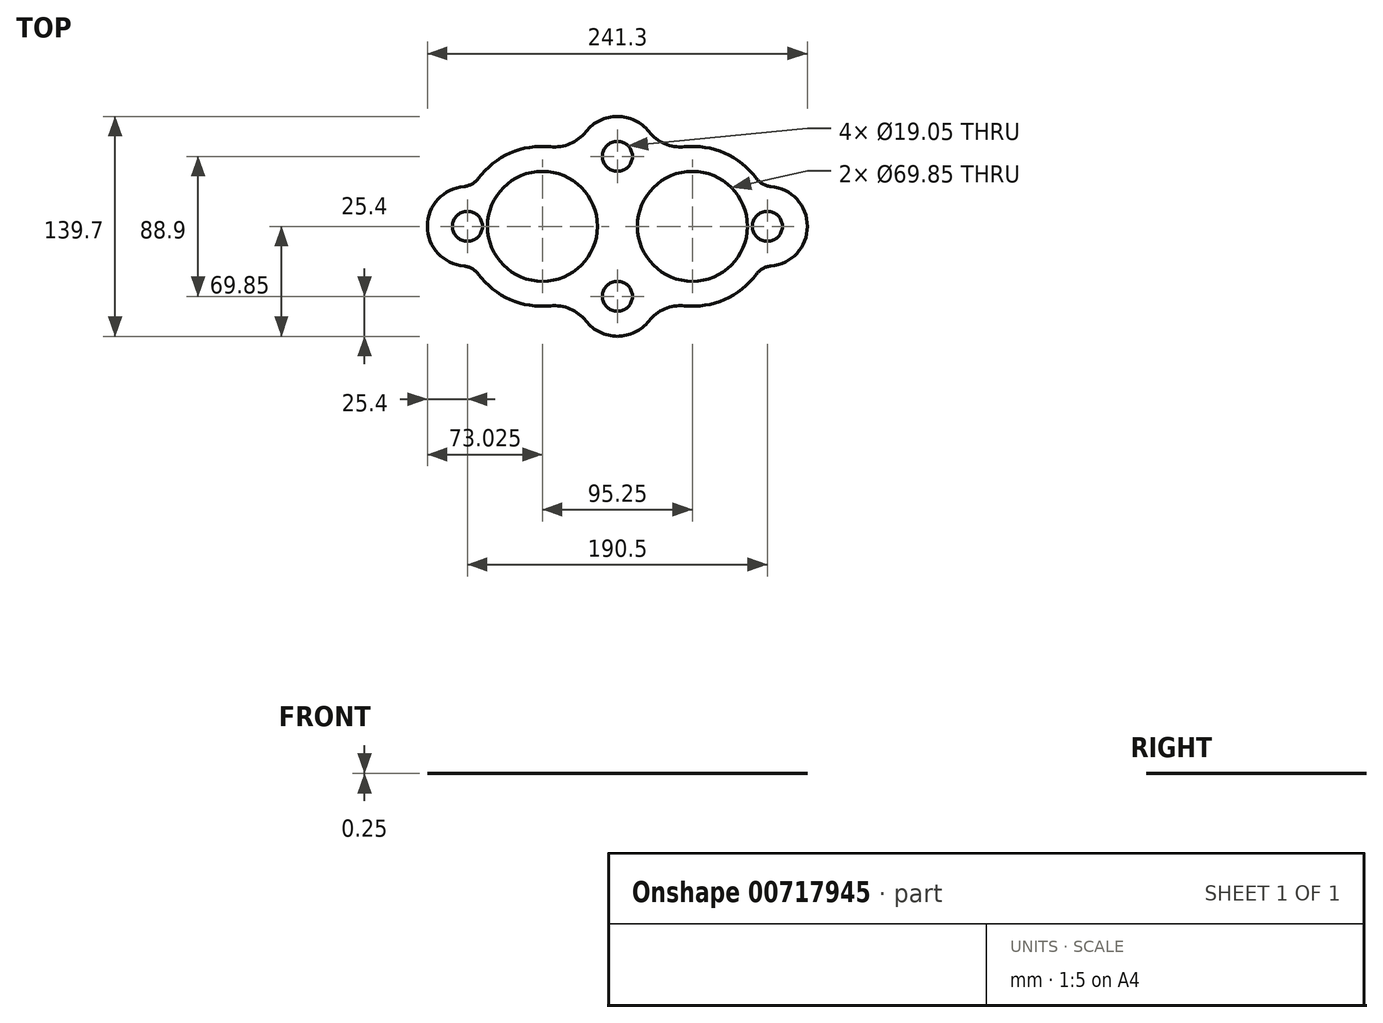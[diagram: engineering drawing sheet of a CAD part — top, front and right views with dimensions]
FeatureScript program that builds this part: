
annotation { "Feature Type Name" : "Feature", "Feature Type Description" : "" }
export const myFeature = defineFeature(function(context is Context, id is Id, definition is map)
    precondition{}
    {
        {
            var Q0;
            Q0=qCreatedBy(makeId("Top.planeOp"),FACE);
            var sketch = newSketch(context, id + "F0", { "sketchPlane" : qUnion([Q0])});
            skCircle(sketch, "E0", {"center": v(-47.63, 0) * mm, "radius": 34.93 * mm});
            skCircle(sketch, "E1", {"center": v(47.63, 0) * mm, "radius": 34.93 * mm});
            skCircle(sketch, "E2", {"center": v(-95.25, 0) * mm, "radius": 9.53 * mm});
            skCircle(sketch, "E3", {"center": v(95.25, 0) * mm, "radius": 9.53 * mm});
            skCircle(sketch, "E4", {"center": v(0, 44.45) * mm, "radius": 9.53 * mm});
            skCircle(sketch, "E5", {"center": v(0, -44.45) * mm, "radius": 9.53 * mm});
            skArc(sketch, "E6", {"start": v(-97.44, -25.3) * mm, "mid": v(-120.65, 0) * mm, "end": v(-97.44, 25.3) * mm});
            skArc(sketch, "E7", {"start": v(-88.35, 30.37) * mm, "mid": v(-68.1, 46.5) * mm, "end": v(-42.52, 50.54) * mm});
            skArc(sketch, "E8", {"start": v(-19.98, 60.13) * mm, "mid": v(0, 69.85) * mm, "end": v(19.98, 60.13) * mm});
            skArc(sketch, "E9", {"start": v(42.52, 50.54) * mm, "mid": v(68.1, 46.5) * mm, "end": v(88.35, 30.37) * mm});
            skArc(sketch, "E10", {"start": v(97.44, 25.3) * mm, "mid": v(120.65, 0) * mm, "end": v(97.44, -25.3) * mm});
            skArc(sketch, "E11", {"start": v(88.35, -30.37) * mm, "mid": v(68.1, -46.5) * mm, "end": v(42.52, -50.54) * mm});
            skArc(sketch, "E12", {"start": v(19.98, -60.13) * mm, "mid": v(0, -69.85) * mm, "end": v(-19.98, -60.13) * mm});
            skArc(sketch, "E13", {"start": v(-42.52, -50.54) * mm, "mid": v(-68.1, -46.5) * mm, "end": v(-88.35, -30.37) * mm});
            skPoint(sketch, "E14.visualSharp", {"position": v(-25.37, 45.67) * mm});
            skArc(sketch, "E14.filletArc", {"start": v(-42.52, 50.54) * mm, "mid": v(-30.02, 52.44) * mm, "end": v(-19.98, 60.13) * mm});
            skPoint(sketch, "E15.visualSharp", {"position": v(25.37, 45.67) * mm});
            skArc(sketch, "E15.filletArc", {"start": v(19.98, 60.13) * mm, "mid": v(30.02, 52.44) * mm, "end": v(42.52, 50.54) * mm});
            skPoint(sketch, "E16.visualSharp", {"position": v(25.37, -45.67) * mm});
            skArc(sketch, "E16.filletArc", {"start": v(42.52, -50.54) * mm, "mid": v(30.02, -52.44) * mm, "end": v(19.98, -60.13) * mm});
            skPoint(sketch, "E17.visualSharp", {"position": v(-25.37, -45.67) * mm});
            skArc(sketch, "E17.filletArc", {"start": v(-19.98, -60.13) * mm, "mid": v(-30.02, -52.44) * mm, "end": v(-42.52, -50.54) * mm});
            skPoint(sketch, "E18.visualSharp", {"position": v(-91.76, -25.16) * mm});
            skArc(sketch, "E18.filletArc", {"start": v(-88.35, -30.37) * mm, "mid": v(-92.35, -26.86) * mm, "end": v(-97.44, -25.3) * mm});
            skPoint(sketch, "E19.visualSharp", {"position": v(91.76, -25.16) * mm});
            skArc(sketch, "E19.filletArc", {"start": v(97.44, -25.3) * mm, "mid": v(92.35, -26.86) * mm, "end": v(88.35, -30.37) * mm});
            skPoint(sketch, "E20.visualSharp", {"position": v(91.76, 25.16) * mm});
            skArc(sketch, "E20.filletArc", {"start": v(88.35, 30.37) * mm, "mid": v(92.35, 26.86) * mm, "end": v(97.44, 25.3) * mm});
            skPoint(sketch, "E21.visualSharp", {"position": v(-91.76, 25.16) * mm});
            skArc(sketch, "E21.filletArc", {"start": v(-97.44, 25.3) * mm, "mid": v(-92.35, 26.86) * mm, "end": v(-88.35, 30.37) * mm});
            skSolve(sketch);
        }
        {
            var Q0;
            Q0=makeQuery(id+"F0.imprint","IMPRINT",FACE,{"disambiguationData":[TD([[makeQuery(id+"F0.imprint","IMPRINT",EDGE,{"derivedFrom":sQuery(id+"F0.wireOp",EDGE,"E0")}),-1.0]])]});
            extrude(context, id + "F1", {"entities" : qUnion([Q0]), "depth" : 0.25 * mm, "offsetDistance" : 25.4 * mm});
        }
    });
